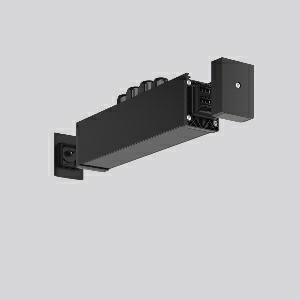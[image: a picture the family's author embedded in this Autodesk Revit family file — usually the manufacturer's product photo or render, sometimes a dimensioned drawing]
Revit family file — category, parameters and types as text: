
# Revit family: linedo_universaleinspeisung_14pol_b_s_982698_003_6_6357
name_source: partatom
category: Lighting Fixtures
units: mm (PartAtom-declared; Revit-internal decimal feet)

## family parameters
Cut with Voids When Loaded = No
Host = Face
Light Source = No
Part Type = Normal
Room Calculation Point = No
Round Connector Dimension = Use Diameter
Shared = No

## types (1)
- LINEDO_Universaleinspeisung_14pol_B_S
    Apparent Load = 0 VA
    Default Elevation = 1800 mm
    Description = Series: LINEDO
Universal power feed that can be used as initial or central feed for flexible installation on site. 14-pole, connection socket / plug. Housing: extruded aluminium profile, powder-coated. Cover made of plastic, surface like housing. LINEDO plug system, plastic, black. Incl. end caps. 4 cable glands (2 x M20 and 2 x M25). Cable glands on top. Easy connection for rigid or flexible wires.
Colour: black
Length: 330 mm
Width: 58 mm
Height: 76 mm
Weight: 913 g
    Height = 76 mm
    Lamp = 0 x
    Length = 330 mm
    Luminous efficacy = 0 lm/W
    Manufacturer = RZB
    ModVariant = No
    Model = 982698.003.6
    Mounting Place = Ceiling
    Mounting Type = Surface mounted
    Number of Poles = 1
    OnlyDefault = Yes
    Power Factor = 1
    Product Name = LINEDO_Universaleinspeisung_14pol_B_S
    Product group = Surface mounted continuous line luminaire system
    ProductGroupID = 310
    Protection Class = Protection class I
    Protection Degree = Degree of protection
    RLX_Detail_Level = 1
    RLX_Emergency_Light_Flux = 0 lm
    RLX_Emergency_Type = 0
    RLX_Emergency_Type_DB = No
    RlxData = <blob elided: 18793 chars, md5=d5d08b8a>
    Standby Power = 0 W
    System Light Flux = 0 lm
    System Power = 0 W
    Type Comments = Product without accessories
    Type Image = 982698.003.6.jpg
    URL = http://relux.com
    VarID = ---
    Voltage = 0 V
    Weight = 0.00 kg
    Width = 58 mm

## geometry (parser evidence)
native form markers: Blend x4, Sweep x12
no freeform markers — native parametric forms only
